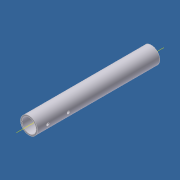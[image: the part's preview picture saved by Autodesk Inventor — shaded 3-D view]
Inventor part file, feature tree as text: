
AUTODESK INVENTOR PART (.ipt)
format: ipt  version: 2012 (Build 160160000, 160)  size: 86,528 bytes
history: native  units: in
note: dims shown in document units (in); Inventor stores cm internally (conversion verified against a paired STEP export)
features: extrude x2, other x2, sketch x2, plane x1, pattern_linear x1, projected_geometry x1
ambient origin geometry x8: Origin, YZ Plane, XZ Plane, XY Plane, X Axis, Y Axis, Z Axis, Center Point
bodies: Solid1 (feature_tree)
feature tree (9):
  extrude  "Extrusion1"  Depth=1.375in
  plane  "Work Plane1"
  extrude  "Extrusion2"  TaperAngle=0.0deg  [1 undecoded]
  other  "Work Axis2"
  pattern_linear  "Rectangular Pattern1"  Spacing1=1.0in  [1 undecoded]
  sketch  "Sketch1"  dims[d0=1.656in d1=1.375in]
  other  "Work Axis1"
  sketch  "Sketch2"  dims[d2=11.875in d3=0.0in d4=0.0in d5=1.0in d6=0.25in d7=2.0in d8=0.0in d9=0.7874in d11=2.0in]
  projected_geometry  "Projected Loop1"
note: 2 required parameter values undecoded (feature->parameter linkage not recoverable at this tier; creation-order binding heuristic only, values carry confidence <= 0.55)
